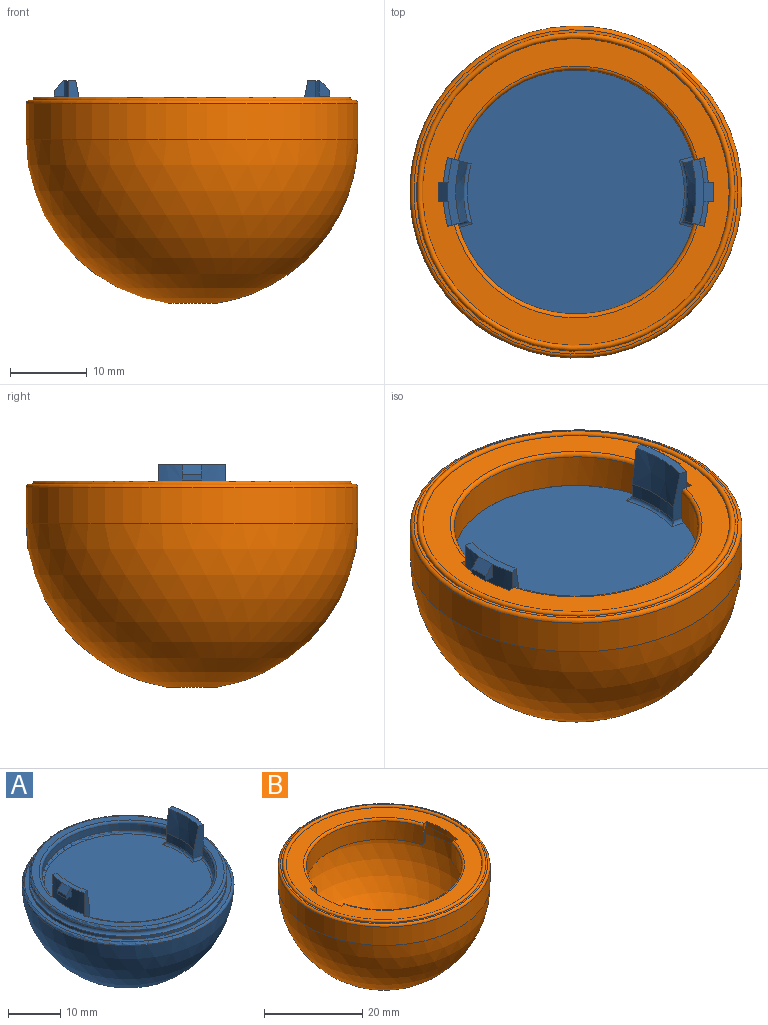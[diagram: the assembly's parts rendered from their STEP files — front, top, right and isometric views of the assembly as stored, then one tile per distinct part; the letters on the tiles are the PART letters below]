
ASSEMBLY  parts=2 mates=1
PART A: 42 faces, bbox 44x44x27.9 mm
  f0: cylinder r=16.51mm len=31.9mm, axis (0,0,1), area 65.9mm2, adj f10,f17,f37,f38
  f1: plane 32x30.77mm, normal (0,0,1), area 771.5mm2, adj f10,f31,f32,f33,f34,f35,f36,f37
  f2: cylinder r=16.51mm len=31.9mm, axis (0,0,1), area 65.9mm2, adj f11,f16,f33,f40
  f3: plane 36.85x36.85mm, normal (0,0,1), area 163.5mm2, adj f9,f10,f11,f15,f16,f17,f38,f40
  f4: plane 39.61x39.61mm, normal (0,0,1), area 106.1mm2, adj f8,f39
  f5: sphere r=20.32mm, area 2527.8mm2, adj f39
  f6: cylinder r=18.93mm len=37.87mm, axis (0,0,1), area 15.1mm2, adj f7,f41
  f7: torus R=18.93mm, axis (0,0,1), area 232.3mm2, adj f6,f8
  f8: cylinder r=18.93mm len=37.87mm, axis (0,0,1), area 75.5mm2, adj f4,f7
  f9: cylinder r=16.64mm len=8.61mm, axis (0,0,1), area 39.1mm2, adj f3,f10,f11,f14,f21,f22,f24
  f10: plane 7.62x2.82mm, normal (0.26,0.97,0), area 12.6mm2, adj f0,f1,f3,f9,f12,f13,f14,f31
  f11: plane 7.11x2.33mm, normal (0.26,-0.97,0), area 11.7mm2, adj f2,f3,f9,f12,f13,f14,f32,f40
  f12: cylinder r=14.61mm len=7.56mm, axis (0,0,1), area 15.5mm2, adj f10,f11,f13,f31
  f13: cone r=15.62mm half-angle=11.3deg, axis (0,0,1), area 41mm2, adj f10,f11,f12,f14
  f14: plane 8.61x1.55mm, normal (0,0,1), area 8.6mm2, adj f9,f10,f11,f13,f21,f22,f25
  f15: cylinder r=16.64mm len=8.61mm, axis (0,0,1), area 39.1mm2, adj f3,f16,f17,f20,f26,f27,f28
  f16: plane 7.11x2.33mm, normal (-0.26,-0.97,0), area 11.7mm2, adj f2,f3,f15,f18,f19,f20,f34,f40
  f17: plane 7.11x2.33mm, normal (-0.26,0.97,0), area 11.7mm2, adj f0,f3,f15,f18,f19,f20,f36,f38
  f18: cone r=15.62mm half-angle=11.3deg, axis (0,0,1), area 41mm2, adj f16,f17,f19,f20
  f19: cylinder r=14.61mm len=7.56mm, axis (0,0,1), area 15.5mm2, adj f16,f17,f18,f35
  f20: plane 8.61x1.55mm, normal (0,0,1), area 8.6mm2, adj f15,f16,f17,f18,f26,f27,f30
  f21: plane 2.03x1.32mm, normal (0,-1,0), area 1.9mm2, adj f9,f14,f23,f24,f25
  f22: plane 2.03x1.32mm, normal (0,1,0), area 1.9mm2, adj f9,f14,f23,f24,f25
  f23: plane 2.54x0.76mm, normal (-1,0,0), area 1.9mm2, adj f21,f22,f24,f25
  f24: plane 2.54x1.32mm, normal (0,0,-1), area 3.3mm2, adj f9,f21,f22,f23
  f25: plane 2.54x1.27mm, normal (-0.71,0,0.71), area 4.6mm2, adj f14,f21,f22,f23
  f26: plane 2.03x1.32mm, normal (0,-1,0), area 1.9mm2, adj f15,f20,f28,f29,f30
  f27: plane 2.03x1.32mm, normal (0,1,0), area 1.9mm2, adj f15,f20,f28,f29,f30
  f28: plane 2.54x1.32mm, normal (0,0,-1), area 3.3mm2, adj f15,f26,f27,f29
  f29: plane 2.54x0.76mm, normal (1,0,0), area 1.9mm2, adj f26,f27,f28,f30
  f30: plane 2.54x1.27mm, normal (0.71,0,0.71), area 4.6mm2, adj f20,f26,f27,f29
  f31: torus R=14.1mm, axis (0,0,1), area 6.2mm2, adj f1,f10,f12,f32
  f32: cylinder r=0.51mm len=2.47mm, axis (0.97,0.26,0), area 1.5mm2, adj f1,f11,f31,f33
  f33: torus R=16mm, axis (0,0,1), area 33.8mm2, adj f1,f2,f32,f34
  f34: cylinder r=0.51mm len=2.47mm, axis (-0.97,0.26,0), area 1.5mm2, adj f1,f16,f33,f35
  f35: torus R=14.1mm, axis (0,0,1), area 6.3mm2, adj f1,f19,f34,f36
  f36: cylinder r=0.51mm len=2.47mm, axis (0.97,0.26,0), area 1.5mm2, adj f1,f17,f35,f37
  f37: torus R=16mm, axis (0,0,1), area 34mm2, adj f0,f1,f10,f36
  f38: torus R=17.02mm, axis (0,0,-1), area 34.9mm2, adj f0,f3,f10,f17
  f39: torus R=19.81mm, axis (0,0,-1), area 102.6mm2, adj f4,f5
  f40: torus R=17.02mm, axis (0,0,-1), area 34.9mm2, adj f2,f3,f11,f16
  f41: torus R=18.43mm, axis (0,0,-1), area 94mm2, adj f3,f6
PART B: 53 faces, bbox 46.8x46.8x26.9 mm
  f0: cylinder r=19.69mm len=39.37mm, axis (0,0,1), area 390.3mm2, adj f9,f10,f47,f48,f49,f50,f51,f52
  f1: cylinder r=17.14mm len=32.84mm, axis (0,0,1), area 116mm2, adj f2,f3,f27,f32,f36,f50,f51,f52
  f2: torus R=16.64mm, axis (0,0,1), area 15.3mm2, adj f1,f16,f33,f51
  f3: torus R=16.64mm, axis (0,0,1), area 15.3mm2, adj f1,f16,f37,f52
  f4: cylinder r=17.14mm len=32.84mm, axis (0,0,1), area 116mm2, adj f5,f6,f24,f40,f45,f47,f48,f49
  f5: torus R=16.64mm, axis (0,0,1), area 15.3mm2, adj f4,f20,f44,f48
  f6: torus R=16.64mm, axis (0,0,1), area 15.3mm2, adj f4,f20,f41,f49
  f7: plane 38.39x38.39mm, normal (0,0,-1), area 183.8mm2, adj f10,f24,f27,f28,f29,f31,f35,f39
  f8: plane 39.88x39.88mm, normal (0,0,1), area 390.1mm2, adj f11,f17,f19,f21,f22,f25,f26,f28
  f9: sphere r=19.69mm, area 2434.7mm2, adj f0,f16,f20
  f10: torus R=19.18mm, axis (0,0,1), area 97.8mm2, adj f0,f7
  f11: torus R=20.32mm, axis (0,0,1), area 152.8mm2, adj f8,f12
  f12: plane 42.16x42.16mm, normal (0,0,1), area 50mm2, adj f11,f30
  f13: cylinder r=21.59mm len=43.18mm, axis (0,0,1), area 620.2mm2, adj f14,f30
  f14: sphere r=21.59mm, area 2899.4mm2, adj f13,f15
  f15: plane 6.1x6.1mm, normal (0,0,-1), area 29.2mm2, adj f14
  f16: plane 31.86x15.09mm, normal (0,0,-1), area 47.2mm2, adj f2,f3,f9,f18,f34,f38,f51,f52
  f17: plane 4.57x1.35mm, normal (-0.26,-0.97,0), area 4.1mm2, adj f8,f18,f26,f29,f31,f32,f34
  f18: cylinder r=15.88mm len=30.67mm, axis (0,0,1), area 189.8mm2, adj f16,f17,f19,f26,f34,f38
  f19: plane 4.57x1.35mm, normal (0.26,-0.97,0), area 4.1mm2, adj f8,f18,f26,f28,f35,f36,f38
  f20: plane 31.86x15.09mm, normal (0,0,-1), area 47.2mm2, adj f5,f6,f9,f23,f42,f43,f48,f49
  f21: plane 4.57x1.35mm, normal (-0.26,0.97,0), area 4.1mm2, adj f8,f23,f25,f29,f43,f45,f46
  f22: plane 4.57x1.35mm, normal (0.26,0.97,0), area 4.1mm2, adj f8,f23,f25,f28,f39,f40,f42
  f23: cylinder r=15.88mm len=30.67mm, axis (0,0,1), area 189.8mm2, adj f20,f21,f22,f25,f42,f43
  f24: torus R=17.65mm, axis (0,0,-1), area 35.4mm2, adj f4,f7,f39,f46
  f25: torus R=16.38mm, axis (0,0,1), area 33.5mm2, adj f8,f21,f22,f23
  f26: torus R=16.38mm, axis (0,0,1), area 33.5mm2, adj f8,f17,f18,f19
  f27: torus R=17.65mm, axis (0,0,-1), area 35.4mm2, adj f1,f7,f31,f35
  f28: cylinder r=17.27mm len=9.28mm, axis (0,0,1), area 11.6mm2, adj f7,f8,f19,f22,f35,f39
  f29: cylinder r=17.27mm len=9.28mm, axis (0,0,1), area 11.6mm2, adj f7,f8,f17,f21,f31,f46
  f30: torus R=21.08mm, axis (0,0,1), area 107.3mm2, adj f12,f13
  f31: bspline ~1.16x1.15mm, area 0.6mm2, adj f7,f17,f27,f29,f32
  f32: cylinder r=0.51mm len=2.79mm, axis (0,0,1), area 2.3mm2, adj f1,f17,f31,f33
  f33: sphere r=0.51mm, area 0.4mm2, adj f2,f32,f34
  f34: cylinder r=0.51mm len=0.87mm, axis (0.97,-0.26,0), area 0.6mm2, adj f16,f17,f18,f33
  f35: bspline ~1.16x1.15mm, area 0.6mm2, adj f7,f19,f27,f28,f36
  f36: cylinder r=0.51mm len=2.79mm, axis (0,0,1), area 2.3mm2, adj f1,f19,f35,f37
  f37: sphere r=0.51mm, area 0.6mm2, adj f3,f36,f38
  f38: cylinder r=0.51mm len=0.87mm, axis (0.97,0.26,0), area 0.6mm2, adj f16,f18,f19,f37
  f39: bspline ~1.16x1.15mm, area 0.6mm2, adj f7,f22,f24,f28,f40
  f40: cylinder r=0.51mm len=2.79mm, axis (0,0,1), area 2.3mm2, adj f4,f22,f39,f41
  f41: sphere r=0.51mm, area 0.4mm2, adj f6,f40,f42
  f42: cylinder r=0.51mm len=0.87mm, axis (-0.97,0.26,0), area 0.6mm2, adj f20,f22,f23,f41
  f43: cylinder r=0.51mm len=0.87mm, axis (-0.97,-0.26,0), area 0.6mm2, adj f20,f21,f23,f44
  f44: sphere r=0.51mm, area 0.4mm2, adj f5,f43,f45
  f45: cylinder r=0.51mm len=2.79mm, axis (0,0,1), area 2.3mm2, adj f4,f21,f44,f46
  f46: bspline ~1.16x1.15mm, area 0.6mm2, adj f7,f21,f24,f29,f45
  f47: plane 5.08x2.73mm, normal (0,0,1), area 12.9mm2, adj f0,f4,f48,f49
  f48: plane 3.11x1.81mm, normal (-1,0,0), area 4.6mm2, adj f0,f4,f5,f20,f47
  f49: plane 3.11x1.81mm, normal (1,0,0), area 4.6mm2, adj f0,f4,f6,f20,f47
  f50: plane 5.08x2.73mm, normal (0,0,1), area 12.9mm2, adj f0,f1,f51,f52
  f51: plane 3.11x1.81mm, normal (-1,0,0), area 4.6mm2, adj f0,f1,f2,f16,f50
  f52: plane 3.11x1.81mm, normal (1,0,0), area 4.6mm2, adj f0,f1,f3,f16,f50
PLACE A t=(-33.12,-11.31,25)mm
PLACE B t=(-33.12,-11.31,25)mm
MATE ball A.f39 <-> B.f11  axis (0,0,1) through (-33.12,-11.31,25)mm
